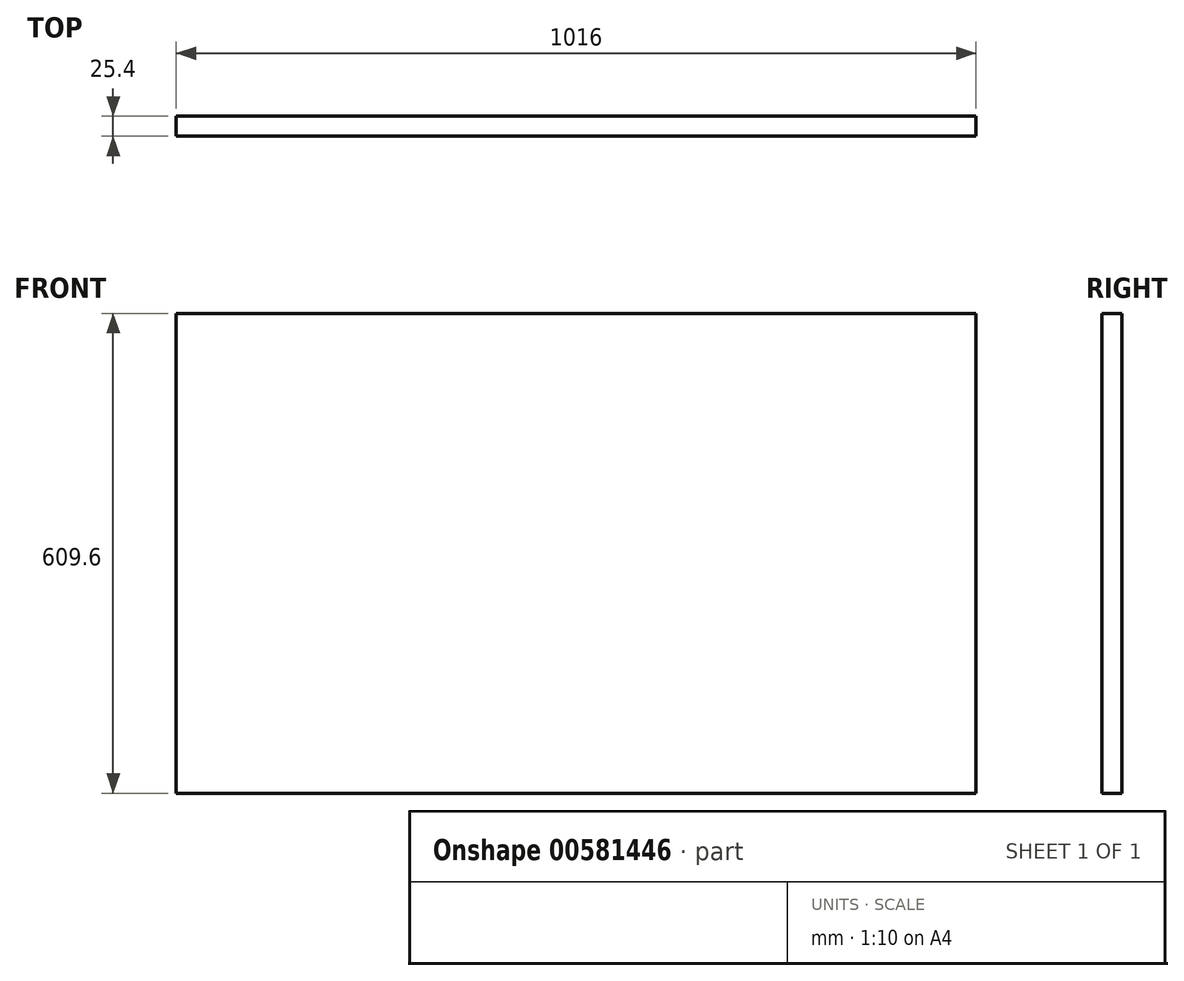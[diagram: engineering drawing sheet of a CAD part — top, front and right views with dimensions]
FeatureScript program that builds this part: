
annotation { "Feature Type Name" : "Feature", "Feature Type Description" : "" }
export const myFeature = defineFeature(function(context is Context, id is Id, definition is map)
    precondition{}
    {
        {
            var Q0;
            Q0=qCreatedBy(makeId("Front.planeOp"),FACE);
            var sketch = newSketch(context, id + "F0", { "sketchPlane" : qUnion([Q0])});
            skLineSegment(sketch, "E0.bottom", {"start": v(-481.12, 349.16) * mm, "end": v(534.88, 349.16) * mm});
            skLineSegment(sketch, "E0.top", {"start": v(-481.12, -260.44) * mm, "end": v(534.88, -260.44) * mm});
            skLineSegment(sketch, "E0.left", {"start": v(-481.12, 349.16) * mm, "end": v(-481.12, -260.44) * mm});
            skLineSegment(sketch, "E0.right", {"start": v(534.88, 349.16) * mm, "end": v(534.88, -260.44) * mm});
            skSolve(sketch);
        }
        {
            var Q0;
            Q0 = qSketchRegion(id + "F0", true);
            extrude(context, id + "F1", {"entities" : qUnion([Q0]), "depth" : 25.4 * mm, "offsetDistance" : 25.4 * mm});
        }
    });
